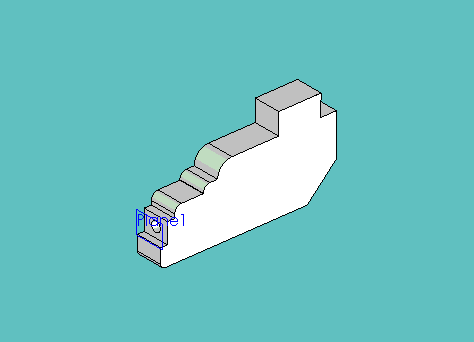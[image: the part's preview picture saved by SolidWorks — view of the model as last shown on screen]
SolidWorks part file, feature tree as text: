
SOLIDWORKS PART (.sldprt)
format: sldprt  version: not decoded by parser v0  size: 892,416 bytes
history: native  units: mm
features: sketch x3, extrude x2, material x1, boolean_combine x1, plane x1, cut_extrude x1 (+11 scaffold rows collapsed)
feature tree (20):
  scaffold x11  (default folders/planes/origin — collapsed)
  material  "Material <not specified>"
  sketch  "Sketch1"  dims[c1.D11=4.7625mm c1.D12=4.7625mm c1.D13=3.175mm c1.D1=20.6502mm c1.D2=4.7625mm c1.D3=~13.49375mm c1.D4=35.56mm c1.D5=5.08mm c1.D6=27.94mm c1.D7=20.32mm c1.D8=40.64mm c1.D9=50.8mm c1.D10=10.16mm c1.D14=33.3375mm c1.D15=15.24mm c1.D16=30.1625mm c1.D17=41.275mm c1.D18=30.1625mm c1.D19=~28.207489mm c2.D19=45.0deg]
  extrude  "Extrude1"  Depth=9.525mm
  sketch  "Sketch3"  dims[D2=7.1374mm D1=20.6502mm]
  extrude  "Extrude2"  Depth=12.7mm
  boolean_combine  "Combine1"
  plane  "Plane1"  Offset=4.7625mm
  sketch  "Sketch4"  dims[c1.D1=7.9375mm c1.D2=7.9375mm c1.D3=~11.333413mm c2.D3=45.0deg c2.D4=~5.55625mm c2.D1=7.9375mm]
  cut_extrude  "Cut-Extrude1"  [1 undecoded]
decode coverage: 5 of 7 modeling features carry decoded parameters
note: ~ marks probable driven/reference dimensions
note: 1 parameter value undecoded
note: suppression state not decoded; provenance and decode notes live in map.json
